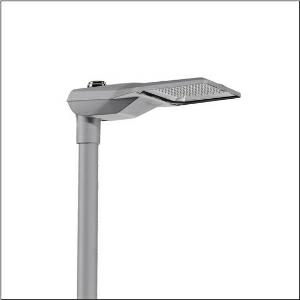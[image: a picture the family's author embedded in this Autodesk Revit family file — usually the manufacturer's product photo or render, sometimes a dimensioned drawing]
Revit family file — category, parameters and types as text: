
# Revit family: streetlight_sl_21_midi___st0_5a_5xe7b37n08lb_6898
name_source: partatom
category: Lighting Fixtures
units: mm (PartAtom-declared; Revit-internal decimal feet)

## family parameters
Cut with Voids When Loaded = No
Host = Face
Light Source = No
Part Type = Normal
Room Calculation Point = No
Round Connector Dimension = Use Diameter
Shared = No

## types (1)
- --- (1 x LED, 14340 lm, 98.3 W, 3000K)
    Apparent Load = 98 VA
    CIE Flux Codes = 41 75 97 100 100
    Color Rendering = 70
    Color Temperature = 3000K
    Default Elevation = 1800 mm
    Description = Streetlight SL 21 midi, mast luminaire, primary light control with lens, of PMMA, primary optical cover: cover, of toughened safety glass, transparent, light distribution: ST0.5a, light emission: direct distribution, primary light characteristic: asymmetric, installation type: side-entry, LED, 3G 2.5mm², High Power LED, rated luminous flux: 14.340lm, luminous efficacy: 146lm/W, light colour: 730, colour temperature: 3000K, control gear: NEMA (7pin), control: overheat protection, pre-setting: linear dimming characteristic, constant luminous flux control, time-dependent luminous flux control, flexible luminous flux parameterisation, mains connection: 220..240V, AC, 50/60Hz, connection cable pre-assembled, cable length: 10,5m, wiring characteristics: H05VV-F, start of lifetime: 98W, end of service life: 101W, reduction: 45W, luminaire housing, of diecast aluminium (EN AC-44300), powder-coated, Siteco® metallic grey (DB 702S), corrosivity category C5 mid according to DIN EN ISO 12944, multi-level sealing system, sealing non-destructively replaceable, inclination adjustable: 0°, 5°, 10°, 15°, length: 644mm, width: 335mm, height: 110mm, spigot size: 42mm (side-entry), mounting height: 4..8m, protection rating (complete): IP66, insulation class (complete): insulation class I (protective earthing), certification: CE, ENEC, ENEC+, VDE, impact resistance: IK10, permissible operating ambient temperature for outdoor applications: -40..+50°C, standard-compliant lighting for roads and squares, packaging unit: 1 piece

Light Distribution: ST0.5a
    Height = 111 mm
    Lamp = 1 x LED
    Lamp Light Flux = 14340 lm
    Lamp Power = 98.3 W
    Lamp count = 1
    Length = 644 mm
    Luminous efficacy = 146 lm/W
    Manufacturer = Siteco
    ModVariant = No
    Model = 5XE7B37N08LB
    Number of Poles = 1
    OnlyDefault = Yes
    Power Factor = 1
    Product Name = Streetlight SL 21 midi | ST0.5a
    Product group = mast luminaire | pylon top
    ProductGroupID = 6100
    Protection Class = Protection class I
    Protection Degree = IP 66
    RLX_Detail_Level = 1
    RLX_Emergency_Light_Flux = 0 lm
    RLX_Emergency_Type = 0
    RLX_Emergency_Type_DB = No
    RlxData = <blob elided: 37685 chars, md5=bc39bb91>
    Socket = socket
    Standby Power = 0 W
    System Light Flux = 14340 lm
    System Power = 98 W
    Type Comments = factory setting: luminous flux: 100 % | dim-lin: 254 | 1020 mA
    Type Image = l_1294377.jpg
    URL = http://relux.com
    VarID = @adj_137378
    Voltage = 0 V
    Weight = 0.00 kg
    Width = 336 mm

## geometry (parser evidence)
native form markers: Blend x4, Sweep x12
no freeform markers — native parametric forms only
